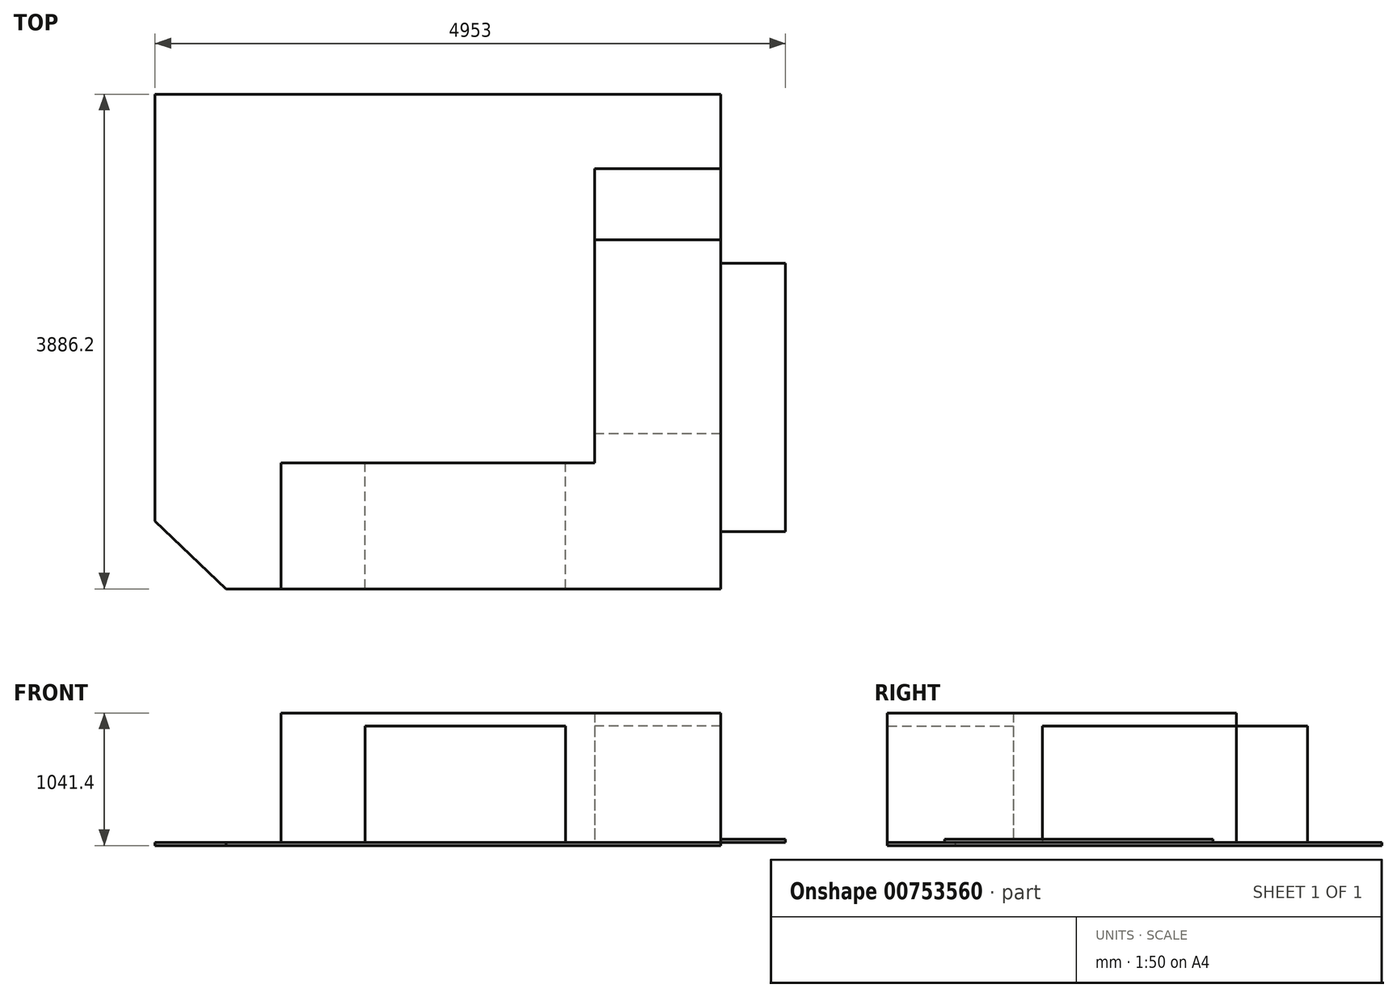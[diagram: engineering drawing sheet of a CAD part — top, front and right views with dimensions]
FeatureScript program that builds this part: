
annotation { "Feature Type Name" : "Feature", "Feature Type Description" : "" }
export const myFeature = defineFeature(function(context is Context, id is Id, definition is map)
    precondition{}
    {
        {
            var Q0;
            Q0=qCreatedBy(makeId("Top.planeOp"),FACE);
            var sketch = newSketch(context, id + "F0", { "sketchPlane" : qUnion([Q0])});
            skLineSegment(sketch, "E0", {"start": v(0, 0) * mm, "end": v(-4445, 0) * mm});
            skLineSegment(sketch, "E1", {"start": v(-4445, 0) * mm, "end": v(-4445, -3352.8) * mm});
            skLineSegment(sketch, "E2", {"start": v(0, 0) * mm, "end": v(0, -3886.2) * mm});
            skLineSegment(sketch, "E3", {"start": v(0, -3886.2) * mm, "end": v(-3886.2, -3886.2) * mm});
            skLineSegment(sketch, "E4", {"start": v(-4445, -3352.8) * mm, "end": v(-3886.2, -3886.2) * mm});
            skSolve(sketch);
        }
        {
            var Q0;
            Q0 = qSketchRegion(id + "F0", true);
            extrude(context, id + "F1", {"entities" : qUnion([Q0]), "depth" : 25.4 * mm, "offsetDistance" : 25.4 * mm});
        }
        {
            var Q0;
            Q0=makeQuery(id+"F1.opExtrude","CAP_FACE",FACE,{"disambiguationData":[OSD([sQuery(id+"F0.wireOp",EDGE,"E0"),sQuery(id+"F0.wireOp",EDGE,"E1"),sQuery(id+"F0.wireOp",EDGE,"E2"),sQuery(id+"F0.wireOp",EDGE,"E3"),sQuery(id+"F0.wireOp",EDGE,"E4")])],"isStart":false});
            var sketch = newSketch(context, id + "F2", { "sketchPlane" : qUnion([Q0])});
            skLineSegment(sketch, "E5.bottom", {"start": v(0, -1327.15) * mm, "end": v(508, -1327.15) * mm});
            skLineSegment(sketch, "E5.top", {"start": v(0, -3435.35) * mm, "end": v(508, -3435.35) * mm});
            skLineSegment(sketch, "E5.left", {"start": v(0, -1327.15) * mm, "end": v(0, -3435.35) * mm});
            skLineSegment(sketch, "E5.right", {"start": v(508, -1327.15) * mm, "end": v(508, -3435.35) * mm});
            skSolve(sketch);
        }
        {
            var Q0;
            Q0 = qSketchRegion(id + "F2", true);
            extrude(context, id + "F3", {"entities" : qUnion([Q0]), "depth" : 25.4 * mm, "offsetDistance" : 25.4 * mm});
        }
        {
            var Q0;
            Q0=makeQuery(id+"F1.opExtrude","CAP_FACE",FACE,{"disambiguationData":[OSD([sQuery(id+"F0.wireOp",EDGE,"E0"),sQuery(id+"F0.wireOp",EDGE,"E1"),sQuery(id+"F0.wireOp",EDGE,"E2"),sQuery(id+"F0.wireOp",EDGE,"E3"),sQuery(id+"F0.wireOp",EDGE,"E4")])],"isStart":false});
            var sketch = newSketch(context, id + "F4", { "sketchPlane" : qUnion([Q0])});
            skLineSegment(sketch, "E6.bottom", {"start": v(-1219.2, -3886.2) * mm, "end": v(-2794, -3886.2) * mm});
            skLineSegment(sketch, "E6.top", {"start": v(-1219.2, -2895.6) * mm, "end": v(-2794, -2895.6) * mm});
            skLineSegment(sketch, "E6.left", {"start": v(-1219.2, -3886.2) * mm, "end": v(-1219.2, -2895.6) * mm});
            skLineSegment(sketch, "E6.right", {"start": v(-2794, -3886.2) * mm, "end": v(-2794, -2895.6) * mm});
            skLineSegment(sketch, "E7.bottom", {"start": v(0, -584.2) * mm, "end": v(-990.6, -584.2) * mm});
            skLineSegment(sketch, "E7.top", {"start": v(0, -2667) * mm, "end": v(-990.6, -2667) * mm});
            skLineSegment(sketch, "E7.left", {"start": v(0, -584.2) * mm, "end": v(0, -2667) * mm});
            skLineSegment(sketch, "E7.right", {"start": v(-990.6, -584.2) * mm, "end": v(-990.6, -2667) * mm});
            skSolve(sketch);
        }
        {
            var Q0;
            Q0 = qSketchRegion(id + "F4", true);
            extrude(context, id + "F5", {"entities" : qUnion([Q0]), "depth" : 914.4 * mm, "offsetDistance" : 25.4 * mm});
        }
        {
            var Q0;
            Q0=makeQuery(id+"F1.opExtrude","CAP_FACE",FACE,{"disambiguationData":[OSD([sQuery(id+"F0.wireOp",EDGE,"E0"),sQuery(id+"F0.wireOp",EDGE,"E1"),sQuery(id+"F0.wireOp",EDGE,"E2"),sQuery(id+"F0.wireOp",EDGE,"E3"),sQuery(id+"F0.wireOp",EDGE,"E4")])],"isStart":false});
            var sketch = newSketch(context, id + "F6", { "sketchPlane" : qUnion([Q0])});
            skLineSegment(sketch, "E8", {"start": v(-3454.4, -3886.2) * mm, "end": v(0, -3886.2) * mm});
            skLineSegment(sketch, "E9", {"start": v(0, -3886.2) * mm, "end": v(0, -1143) * mm});
            skLineSegment(sketch, "E10", {"start": v(0, -1143) * mm, "end": v(-990.6, -1143) * mm});
            skLineSegment(sketch, "E11", {"start": v(-990.6, -1143) * mm, "end": v(-990.6, -2895.6) * mm});
            skLineSegment(sketch, "E12", {"start": v(-990.6, -2895.6) * mm, "end": v(-3454.4, -2895.6) * mm});
            skLineSegment(sketch, "E13", {"start": v(-3454.4, -2895.6) * mm, "end": v(-3454.4, -3886.2) * mm});
            skSolve(sketch);
        }
        {
            var Q0;
            Q0 = qSketchRegion(id + "F6", true);
            extrude(context, id + "F7", {"entities" : qUnion([Q0]), "depth" : 1016 * mm, "offsetDistance" : 25.4 * mm});
        }
    });
